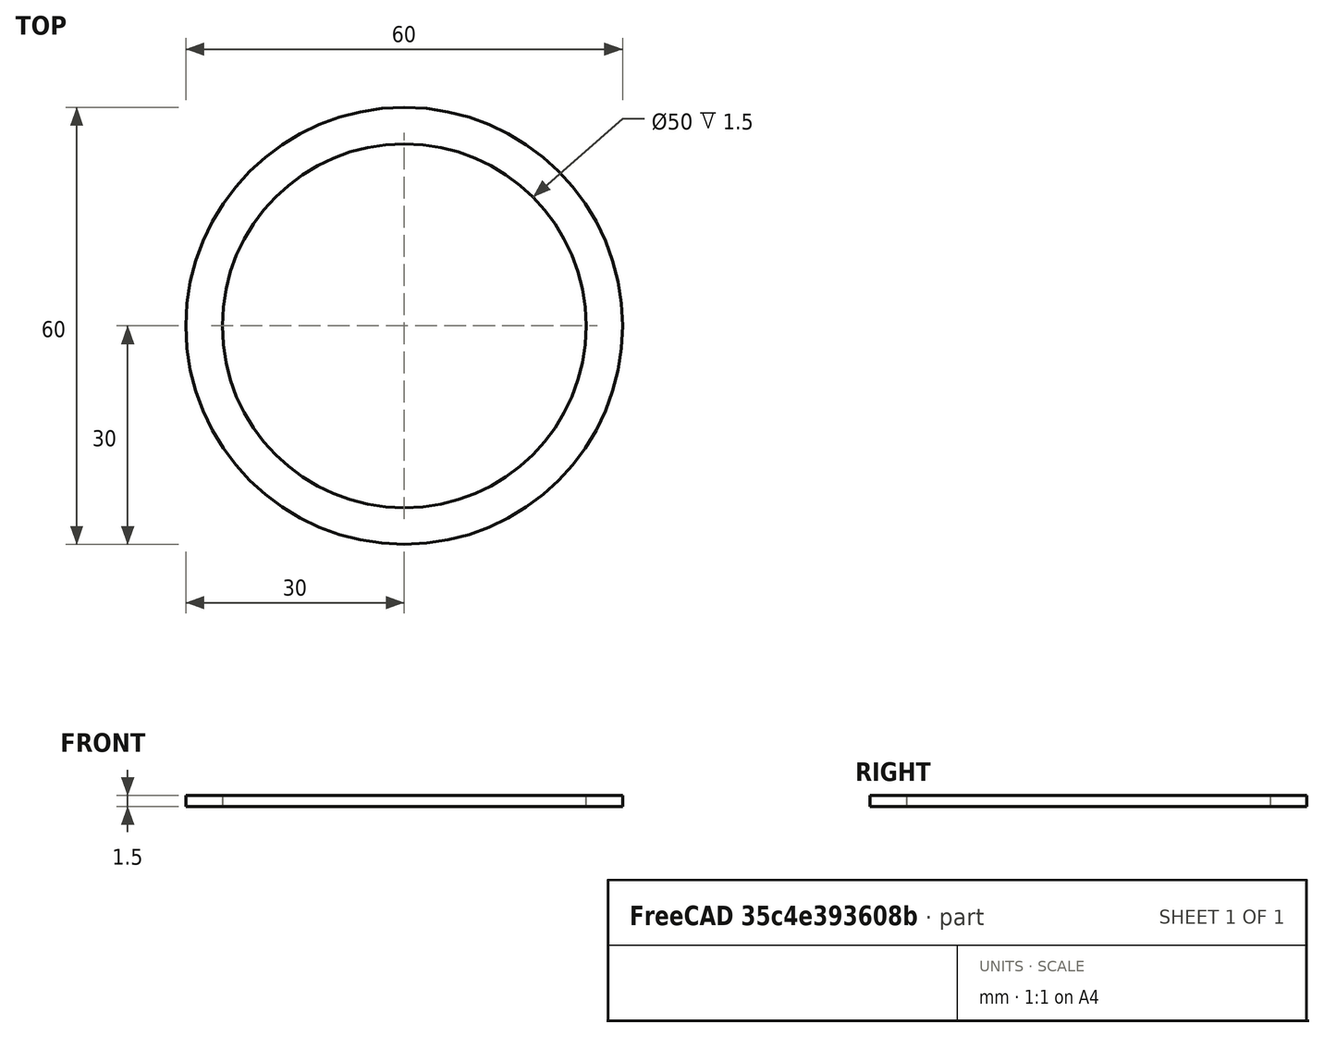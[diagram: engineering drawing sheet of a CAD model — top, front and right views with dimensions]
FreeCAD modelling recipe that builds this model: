
FCSTD DOCUMENT  (FreeCAD 0.19R24276 (Git))
Label: Seal_bear_add_d50_d60
License: All rights reserved
LicenseURL: http://en.wikipedia.org/wiki/All_rights_reserved
objects: Sketcher::SketchObject×1, PartDesign::Pad×1, PartDesign::Body×1
note: 4 computed .brp shape members not serialized (recipe doc carries the construction recipe); baked Part::Feature solids carry a one-line shape summary decoded from their .brp

FEATURE [Sketcher::SketchObject] Sketch  label="Sketch_d50_d60"
  FullyConstrained = true
  MapMode = 5
  Support = -> [XY_Plane]
  sketch-geometry (2):
    g0: Circle CenterX=0 CenterY=0 CenterZ=0 NormalX=0 NormalY=0 NormalZ=1 AngleXU=0 Radius=30
    g1: Circle CenterX=0 CenterY=0 CenterZ=0 NormalX=0 NormalY=0 NormalZ=1 AngleXU=0 Radius=25
  constraints (4):
    c: Coincident(g0,g-1)
    c: Coincident(g1,g0)
    c: Diameter(g0) = 60
    c: Diameter(g1) = 50
FEATURE [PartDesign::Pad] Pad  label="Pad_h1,5"
  Direction = (1,1,1)
  Length = 1.5
  Length2 = 100
  Profile = -> Sketch
  Type = 0
FEATURE [PartDesign::Body] Body
  Group = -> [Sketch,Pad]
  Origin = -> Origin
  Tip = -> Pad
